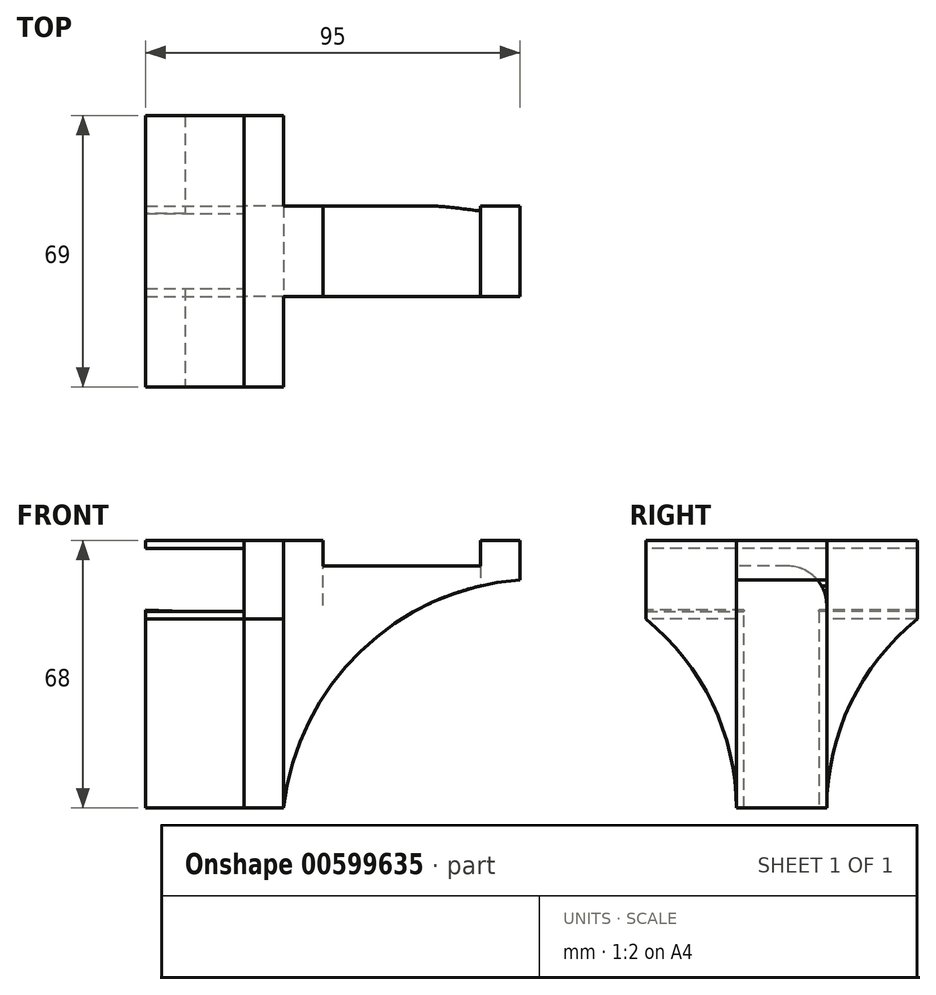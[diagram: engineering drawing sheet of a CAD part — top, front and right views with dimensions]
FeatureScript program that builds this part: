
annotation { "Feature Type Name" : "Feature", "Feature Type Description" : "" }
export const myFeature = defineFeature(function(context is Context, id is Id, definition is map)
    precondition{}
    {
        {
            var Q0;
            Q0=qCreatedBy(makeId("Right.planeOp"),FACE);
            var sketch = newSketch(context, id + "F0", { "sketchPlane" : qUnion([Q0])});
            skLineSegment(sketch, "E0", {"start": v(9.5, 8) * mm, "end": v(34.5, 8) * mm});
            skLineSegment(sketch, "E1", {"start": v(-9.5, 8) * mm, "end": v(-34.5, 8) * mm});
            skLineSegment(sketch, "E2", {"start": v(-34.5, -8) * mm, "end": v(-9.5, -8) * mm});
            skLineSegment(sketch, "E3", {"start": v(-9.5, -58) * mm, "end": v(-9.5, -8) * mm});
            skLineSegment(sketch, "E4", {"start": v(9.5, -8) * mm, "end": v(9.5, -58) * mm});
            skLineSegment(sketch, "E5", {"start": v(9.5, -58) * mm, "end": v(9.5, -8) * mm});
            skLineSegment(sketch, "E6", {"start": v(34.5, -8) * mm, "end": v(9.5, -8) * mm});
            skLineSegment(sketch, "E7", {"start": v(-9.5, -8) * mm, "end": v(9.5, 8) * mm, "construction": true});
            skLineSegment(sketch, "E8", {"start": v(9.5, 8) * mm, "end": v(-9.5, 8) * mm, "construction": true});
            skLineSegment(sketch, "E9", {"start": v(9.5, 8) * mm, "end": v(9.5, -8) * mm, "construction": true});
            skLineSegment(sketch, "E10", {"start": v(9.5, -58) * mm, "end": v(-9.5, -58) * mm});
            skLineSegment(sketch, "E11", {"start": v(-11.5, -58) * mm, "end": v(-9.5, -58) * mm});
            skLineSegment(sketch, "E12", {"start": v(9.5, -58) * mm, "end": v(11.5, -58) * mm});
            skLineSegment(sketch, "E13", {"start": v(11.5, -58) * mm, "end": v(11.5, -10) * mm});
            skLineSegment(sketch, "E14", {"start": v(-34.5, 8) * mm, "end": v(-34.5, 10) * mm});
            skLineSegment(sketch, "E15", {"start": v(34.5, 10) * mm, "end": v(34.5, 8) * mm});
            skLineSegment(sketch, "E16", {"start": v(34.5, -8) * mm, "end": v(34.5, -10) * mm});
            skLineSegment(sketch, "E17", {"start": v(34.5, -10) * mm, "end": v(11.5, -10) * mm});
            skLineSegment(sketch, "E18", {"start": v(-34.5, -10) * mm, "end": v(-34.5, -8) * mm});
            skLineSegment(sketch, "E19.trimOffspring", {"start": v(-9.5, 10) * mm, "end": v(9.5, 10) * mm});
            skLineSegment(sketch, "E20.trimOffspring", {"start": v(-11.5, -10) * mm, "end": v(-11.5, -58) * mm});
            skLineSegment(sketch, "E21.trimOffspring", {"start": v(-11.5, -10) * mm, "end": v(-34.5, -10) * mm});
            skArc(sketch, "E22", {"start": v(34.5, -10) * mm, "mid": v(17.55, -31.39) * mm, "end": v(11.5, -58) * mm});
            skArc(sketch, "E23", {"start": v(-11.5, -58) * mm, "mid": v(-17.55, -31.39) * mm, "end": v(-34.5, -10) * mm});
            skLineSegment(sketch, "E24", {"start": v(-34.5, 8) * mm, "end": v(-34.5, -8) * mm});
            skLineSegment(sketch, "E25", {"start": v(34.5, 8) * mm, "end": v(34.5, -8) * mm});
            skLineSegment(sketch, "E26", {"start": v(9.5, -8) * mm, "end": v(-9.5, -8) * mm, "construction": true});
            skLineSegment(sketch, "E27", {"start": v(-34.5, 10) * mm, "end": v(-9.5, 10) * mm});
            skLineSegment(sketch, "E28", {"start": v(9.5, 10) * mm, "end": v(34.5, 10) * mm});
            skLineSegment(sketch, "E29", {"start": v(9.5, 8) * mm, "end": v(-9.5, 8) * mm});
            skSolve(sketch);
        }
        {
            var Q0;
            {var subQ6=sQuery(id+"F0.wireOp",EDGE,"K90TnNzw-sn8z-8ZcA-jQ63-fdc7ie6eovS4");Q0=makeQuery(id+"F0.imprint","IMPRINT",FACE,{"disambiguationData":[TD([[makeQuery(id+"F0.imprint","IMPRINT",EDGE,{"derivedFrom":subQ6}),1.0]])]});}
            var Q1;
            {var subQ3=sQuery(id+"F0.wireOp",EDGE,"vnbRwp2E-X7cf-orMJ-CY1s-ikwOvejmN5t4");Q1=makeQuery(id+"F0.imprint","IMPRINT",FACE,{"disambiguationData":[TD([[makeQuery(id+"F0.imprint","IMPRINT",EDGE,{"derivedFrom":subQ3}),1.0]])]});}
            var Q2;
            {var subQ4=sQuery(id+"F0.wireOp",EDGE,"E11");Q2=makeQuery(id+"F0.imprint","IMPRINT",FACE,{"disambiguationData":[TD([[makeQuery(id+"F0.imprint","IMPRINT",EDGE,{"derivedFrom":subQ4}),1.0]])]});}
            var Q3;
            {var subQ6=sQuery(id+"F0.wireOp",EDGE,"E12");Q3=makeQuery(id+"F0.imprint","IMPRINT",FACE,{"disambiguationData":[TD([[makeQuery(id+"F0.imprint","IMPRINT",EDGE,{"derivedFrom":subQ6}),1.0]])]});}
            var Q4;
            Q4=makeQuery(id+"F0.imprint","IMPRINT",FACE,{"disambiguationData":[TD([[makeQuery(id+"F0.imprint","IMPRINT",EDGE,{"derivedFrom":sQuery(id+"F0.wireOp",EDGE,"E0")}),1.0]])]});
            extrude(context, id + "F1", {"entities" : qUnion([Q0, Q1, Q2, Q3, Q4]), "oppositeDirection" : true, "depth" : 25 * mm, "offsetDistance" : 25 * mm});
        }
        {
            var Q0;
            Q0=makeQuery(id+"F0.imprint","IMPRINT",FACE,{"disambiguationData":[TD([[makeQuery(id+"F0.imprint","IMPRINT",EDGE,{"derivedFrom":sQuery(id+"F0.wireOp",EDGE,"oMMupTnJ-5dAi-IWF1-EToU-SHisiRkZDjAE")}),-1.0]])]});
            var Q1;
            {var subQ0=sQuery(id+"F0.wireOp",EDGE,"Qg3MfWCu-p63A-8WpK-BNXs-PRB2UsBoB1dU");Q1=makeQuery(id+"F0.imprint","IMPRINT",FACE,{"disambiguationData":[TD([[makeQuery(id+"F0.imprint","IMPRINT",EDGE,{"derivedFrom":subQ0}),-1.0]])]});}
            var Q2;
            Q2=makeQuery(id+"F0.imprint","IMPRINT",FACE,{"disambiguationData":[TD([[makeQuery(id+"F0.imprint","IMPRINT",EDGE,{"derivedFrom":sQuery(id+"F0.wireOp",EDGE,"c29069f4-b1cd-42a6-91a8-be57f884039c.trimOffspring")}),1.0]])]});
            var Q3;
            {var subQ2=sQuery(id+"F0.wireOp",EDGE,"df594554-55b8-4662-abf6-eb507b0dfb9d.trimOffspring");Q3=makeQuery(id+"F0.imprint","IMPRINT",FACE,{"disambiguationData":[TD([[makeQuery(id+"F0.imprint","IMPRINT",EDGE,{"derivedFrom":subQ2}),-1.0]])]});}
            var Q4;
            Q4=makeQuery(id+"F0.imprint","IMPRINT",FACE,{"disambiguationData":[TD([[makeQuery(id+"F0.imprint","IMPRINT",EDGE,{"derivedFrom":sQuery(id+"F0.wireOp",EDGE,"E13")}),-1.0]])]});
            var Q5;
            {var subQ0=sQuery(id+"F0.wireOp",EDGE,"E10");Q5=makeQuery(id+"F0.imprint","IMPRINT",FACE,{"disambiguationData":[TD([[makeQuery(id+"F0.imprint","IMPRINT",EDGE,{"derivedFrom":subQ0}),-1.0]])]});}
            var Q6;
            Q6=makeQuery(id+"F0.imprint","IMPRINT",FACE,{"disambiguationData":[TD([[makeQuery(id+"F0.imprint","IMPRINT",EDGE,{"derivedFrom":sQuery(id+"F0.wireOp",EDGE,"E20.trimOffspring")}),-1.0]])]});
            var Q7;
            {var subQ2=sQuery(id+"F0.wireOp",EDGE,"b1d6a6ca-1e82-411d-96f0-e1d4ac3a859d.trimOffspring");Q7=makeQuery(id+"F0.imprint","IMPRINT",FACE,{"disambiguationData":[TD([[makeQuery(id+"F0.imprint","IMPRINT",EDGE,{"derivedFrom":subQ2}),-1.0]])]});}
            var Q8;
            {var subQ0=sQuery(id+"F0.wireOp",EDGE,"b1d6a6ca-1e82-411d-96f0-e1d4ac3a859d.trimOffspring");Q8=makeQuery(id+"F0.imprint","IMPRINT",FACE,{"disambiguationData":[TD([[makeQuery(id+"F0.imprint","IMPRINT",EDGE,{"derivedFrom":subQ0}),1.0]])]});}
            var Q9;
            {var subQ3=sQuery(id+"F0.wireOp",EDGE,"vnbRwp2E-X7cf-orMJ-CY1s-ikwOvejmN5t4");Q9=makeQuery(id+"F0.imprint","IMPRINT",FACE,{"disambiguationData":[TD([[makeQuery(id+"F0.imprint","IMPRINT",EDGE,{"derivedFrom":subQ3}),1.0]])]});}
            var Q10;
            {var subQ6=sQuery(id+"F0.wireOp",EDGE,"K90TnNzw-sn8z-8ZcA-jQ63-fdc7ie6eovS4");Q10=makeQuery(id+"F0.imprint","IMPRINT",FACE,{"disambiguationData":[TD([[makeQuery(id+"F0.imprint","IMPRINT",EDGE,{"derivedFrom":subQ6}),1.0]])]});}
            var Q11;
            {var subQ4=sQuery(id+"F0.wireOp",EDGE,"E11");Q11=makeQuery(id+"F0.imprint","IMPRINT",FACE,{"disambiguationData":[TD([[makeQuery(id+"F0.imprint","IMPRINT",EDGE,{"derivedFrom":subQ4}),1.0]])]});}
            var Q12;
            {var subQ6=sQuery(id+"F0.wireOp",EDGE,"E12");Q12=makeQuery(id+"F0.imprint","IMPRINT",FACE,{"disambiguationData":[TD([[makeQuery(id+"F0.imprint","IMPRINT",EDGE,{"derivedFrom":subQ6}),1.0]])]});}
            var Q13;
            Q13=makeQuery(id+"F0.imprint","IMPRINT",FACE,{"disambiguationData":[TD([[makeQuery(id+"F0.imprint","IMPRINT",EDGE,{"derivedFrom":sQuery(id+"F0.wireOp",EDGE,"E0")}),1.0]])]});
            extrude(context, id + "F2", {"entities" : qUnion([Q0, Q1, Q2, Q3, Q4, Q5, Q6, Q7, Q8, Q9, Q10, Q11, Q12, Q13]), "depth" : 10 * mm, "offsetDistance" : 25 * mm});
        }
        {
            var Q0;
            Q0=makeQuery(id+"F2.opExtrude","CAP_FACE",FACE,{"disambiguationData":[OSD([sQuery(id+"F0.wireOp",EDGE,"Qg3MfWCu-p63A-8WpK-BNXs-PRB2UsBoB1dU"),sQuery(id+"F0.wireOp",EDGE,"E10"),sQuery(id+"F0.wireOp",EDGE,"vnbRwp2E-X7cf-orMJ-CY1s-ikwOvejmN5t4"),sQuery(id+"F0.wireOp",EDGE,"E11"),sQuery(id+"F0.wireOp",EDGE,"E12"),sQuery(id+"F0.wireOp",EDGE,"K90TnNzw-sn8z-8ZcA-jQ63-fdc7ie6eovS4"),sQuery(id+"F0.wireOp",EDGE,"E14"),sQuery(id+"F0.wireOp",EDGE,"E15"),sQuery(id+"F0.wireOp",EDGE,"E16"),sQuery(id+"F0.wireOp",EDGE,"E18"),sQuery(id+"F0.wireOp",EDGE,"QLWsTcF2-cTMP-eXFP-whhu-RSWvKgI9axbR"),sQuery(id+"F0.wireOp",EDGE,"brS6TYGD-zueQ-zvvW-ZPVd-P7JDkevPjVAb"),sQuery(id+"F0.wireOp",EDGE,"E22"),sQuery(id+"F0.wireOp",EDGE,"E23"),sQuery(id+"F0.wireOp",EDGE,"E24"),sQuery(id+"F0.wireOp",EDGE,"E25")])],"isStart":false});
            var sketch = newSketch(context, id + "F3", { "sketchPlane" : qUnion([Q0])});
            skLineSegment(sketch, "E30.0", {"start": v(3.96, -50) * mm, "end": v(-3.96, -50) * mm});
            skArc(sketch, "E30.1", {"start": v(26.5, -6.3) * mm, "mid": v(11.24, -26.1) * mm, "end": v(3.96, -50) * mm});
            skArc(sketch, "E30.2", {"start": v(-3.96, -50) * mm, "mid": v(-11.24, -26.1) * mm, "end": v(-26.5, -6.3) * mm});
            skLineSegment(sketch, "E30.3", {"start": v(26.5, 2.57) * mm, "end": v(26.5, -6.3) * mm});
            skLineSegment(sketch, "E30.4", {"start": v(-26.5, 2.57) * mm, "end": v(-26.5, -6.3) * mm});
            skLineSegment(sketch, "E31", {"start": v(-26.5, 2.57) * mm, "end": v(26.5, 2.57) * mm});
            skSolve(sketch);
        }
        {
            var Q0;
            Q0=makeQuery(id+"F1.opExtrude","SWEPT_FACE",FACE,{"disambiguationData":[OSD([sQuery(id+"F0.wireOp",EDGE,"E18")])]});
            var sketch = newSketch(context, id + "F4", { "sketchPlane" : qUnion([Q0])});
            skLineSegment(sketch, "E32", {"start": v(-25, -8) * mm, "end": v(-25, -7.6) * mm});
            skLineSegment(sketch, "E33", {"start": v(-25, -7.6) * mm, "end": v(-15, -8) * mm});
            skLineSegment(sketch, "E34", {"start": v(-15, -8) * mm, "end": v(-25, -8) * mm});
            skSolve(sketch);
        }
        {
            var Q0;
            Q0 = qSketchRegion(id + "F4", true);
            extrude(context, id + "F5", {"entities" : qUnion([Q0]), "oppositeDirection" : true, "depth" : 69 * mm, "offsetDistance" : 25 * mm});
        }
        {
            var Q0;
            Q0=makeQuery(id+"F1.opExtrude","CAP_FACE",FACE,{"disambiguationData":[OSD([sQuery(id+"F0.wireOp",EDGE,"E5"),sQuery(id+"F0.wireOp",EDGE,"E6"),sQuery(id+"F0.wireOp",EDGE,"E12"),sQuery(id+"F0.wireOp",EDGE,"E13"),sQuery(id+"F0.wireOp",EDGE,"E16"),sQuery(id+"F0.wireOp",EDGE,"E17")])],"isStart":false});
            var sketch = newSketch(context, id + "F6", { "sketchPlane" : qUnion([Q0])});
            skLineSegment(sketch, "E35", {"start": v(-9.5, -8) * mm, "end": v(-9.5, -6.5) * mm});
            skLineSegment(sketch, "E36", {"start": v(-9.5, -6.5) * mm, "end": v(9.5, -6.5) * mm});
            skLineSegment(sketch, "E37", {"start": v(9.5, -6.5) * mm, "end": v(9.5, -8) * mm});
            skLineSegment(sketch, "E38", {"start": v(9.5, -8) * mm, "end": v(-9.5, -8) * mm});
            skSolve(sketch);
        }
        {
            var Q0;
            Q0=makeQuery(id+"F6.imprint","IMPRINT",FACE,{"disambiguationData":[TD([[makeQuery(id+"F6.imprint","IMPRINT",EDGE,{"derivedFrom":sQuery(id+"F6.wireOp",EDGE,"E35")}),-1.0]])]});
            extrude(context, id + "F7", {"entities" : qUnion([Q0]), "operationType" : NewBodyOperationType.REMOVE, "oppositeDirection" : true, "depth" : 10 * mm, "offsetDistance" : 25 * mm});
        }
        {
            var Q0;
            Q0=makeQuery(id+"F3.imprint","IMPRINT",FACE,{"disambiguationData":[TD([[makeQuery(id+"F3.imprint","IMPRINT",EDGE,{"derivedFrom":sQuery(id+"F3.wireOp",EDGE,"E30.0")}),1.0]])]});
            var sketch = newSketch(context, id + "F8", { "sketchPlane" : qUnion([Q0])});
            skLineSegment(sketch, "E39.bottom", {"start": v(-11.5, -58) * mm, "end": v(11.5, -58) * mm});
            skLineSegment(sketch, "E39.top", {"start": v(-11.5, 10) * mm, "end": v(11.5, 10) * mm});
            skLineSegment(sketch, "E39.left", {"start": v(-11.5, -58) * mm, "end": v(-11.5, 10) * mm});
            skLineSegment(sketch, "E39.right", {"start": v(11.5, -58) * mm, "end": v(11.5, 10) * mm});
            skSolve(sketch);
        }
        {
            var Q0;
            Q0 = qSketchRegion(id + "F8", true);
            extrude(context, id + "F9", {"entities" : qUnion([Q0]), "operationType" : NewBodyOperationType.ADD, "depth" : 100 * mm, "offsetDistance" : 25 * mm});
        }
        {
            var Q0;
            Q0=makeQuery(id+"F9.opExtrude","SWEPT_FACE",FACE,{"disambiguationData":[OSD([sQuery(id+"F8.wireOp",EDGE,"E39.left")])]});
            var sketch = newSketch(context, id + "F10", { "sketchPlane" : qUnion([Q0])});
            skLineSegment(sketch, "E40", {"start": v(60, 10) * mm, "end": v(60, 3.5) * mm});
            skLineSegment(sketch, "E41", {"start": v(60, 3.5) * mm, "end": v(20, 3.5) * mm});
            skLineSegment(sketch, "E42", {"start": v(20, 3.5) * mm, "end": v(20, 10) * mm});
            skLineSegment(sketch, "E43", {"start": v(20, 10) * mm, "end": v(60, 10) * mm});
            skLineSegment(sketch, "E44", {"start": v(70, 0) * mm, "end": v(60, 0) * mm, "construction": true});
            skLineSegment(sketch, "E45", {"start": v(60, 3.5) * mm, "end": v(60, 0) * mm, "construction": true});
            skArc(sketch, "E46", {"start": v(70, 0) * mm, "mid": v(29.52, -18.16) * mm, "end": v(10, -58) * mm});
            skLineSegment(sketch, "E47", {"start": v(20, 10) * mm, "end": v(0, 10) * mm});
            skLineSegment(sketch, "E48", {"start": v(70, 0) * mm, "end": v(70, 10) * mm});
            skLineSegment(sketch, "E49", {"start": v(70, 10) * mm, "end": v(60, 10) * mm});
            skLineSegment(sketch, "E50", {"start": v(10, -58) * mm, "end": v(110, -58) * mm});
            skLineSegment(sketch, "E51", {"start": v(110, -58) * mm, "end": v(110, 10) * mm});
            skLineSegment(sketch, "E52", {"start": v(110, 10) * mm, "end": v(70, 10) * mm});
            skSolve(sketch);
        }
        {
            var Q0;
            Q0 = qSketchRegion(id + "F10", true);
            extrude(context, id + "F11", {"entities" : qUnion([Q0]), "operationType" : NewBodyOperationType.REMOVE, "endBound" : BoundingType.THROUGH_ALL, "oppositeDirection" : true, "depth" : 25 * mm, "offsetDistance" : 25 * mm});
        }
        {
            var Q0;
            Q0 = qSketchRegion(id + "F10", true);
            extrude(context, id + "F12", {"entities" : qUnion([Q0]), "operationType" : NewBodyOperationType.REMOVE, "endBound" : BoundingType.THROUGH_ALL, "depth" : 25 * mm, "offsetDistance" : 25 * mm});
        }
        {
            var Q0;
            Q0=makeQuery(id+"F11.boolean.opBoolean","INTERSECT",EDGE,{"derivedFrom":[makeQuery(id+"F9.opExtrude","SWEPT_FACE",FACE,{"disambiguationData":[OSD([sQuery(id+"F8.wireOp",EDGE,"E39.right")])]}),makeQuery(id+"F11.opExtrude","SWEPT_FACE",FACE,{"disambiguationData":[OSD([sQuery(id+"F10.wireOp",EDGE,"E41")])]})]});
            var Q1;
            Q1=makeQuery(id+"F11.boolean.opBoolean","COPY",EDGE,{"derivedFrom":makeQuery(id+"F11.opExtrude","CAP_EDGE",EDGE,{"disambiguationData":[OSD([sQuery(id+"F10.wireOp",EDGE,"E41")])],"isStart":true})});
            fillet(context, id + "F13", {"entities" : qUnion([Q0, Q1]), "radius" : 10 * mm, "tangentPropagation" : true, "allowEdgeOverflow" : false});
        }
    });
